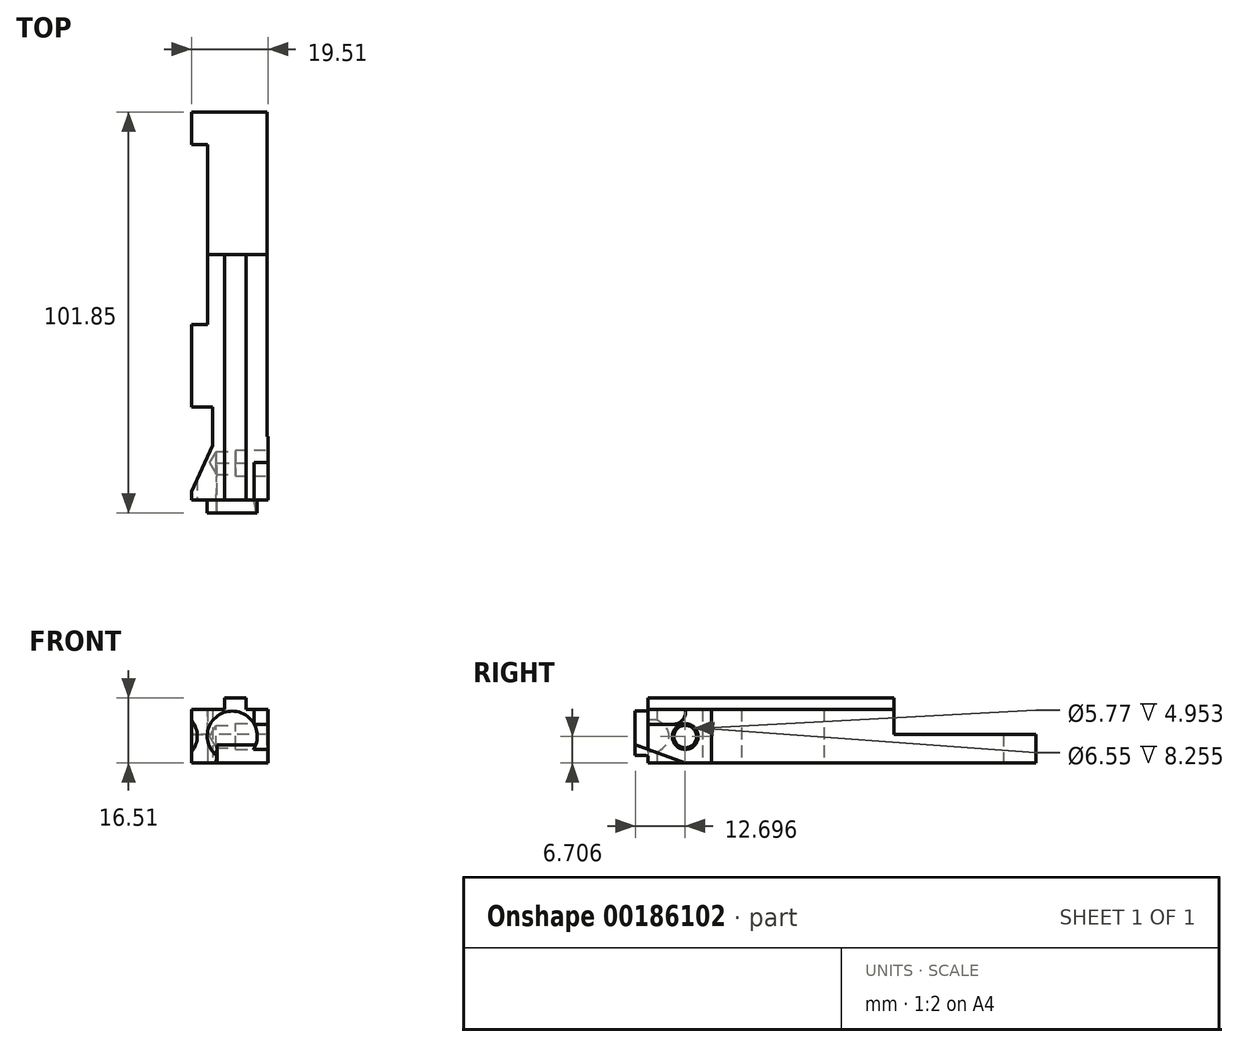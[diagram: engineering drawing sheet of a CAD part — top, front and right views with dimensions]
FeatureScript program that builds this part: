
annotation { "Feature Type Name" : "Feature", "Feature Type Description" : "" }
export const myFeature = defineFeature(function(context is Context, id is Id, definition is map)
    precondition{}
    {
        {
            var Q0;
            Q0=qCreatedBy(makeId("Front.planeOp"),FACE);
            var sketch = newSketch(context, id + "F11", { "sketchPlane" : qUnion([Q0])});
            skLineSegment(sketch, "E0.bottom", {"start": v(0, 0) * mm, "end": v(19.25, 0) * mm});
            skLineSegment(sketch, "E0.top", {"start": v(0, -16.51) * mm, "end": v(19.25, -16.51) * mm});
            skLineSegment(sketch, "E0.left", {"start": v(0, 0) * mm, "end": v(0, -16.51) * mm});
            skLineSegment(sketch, "E0.right", {"start": v(19.25, 0) * mm, "end": v(19.25, -16.51) * mm});
            skSolve(sketch);
        }
        {
            var Q0;
            Q0=makeQuery(id+"F11.imprint","IMPRINT",FACE,{"disambiguationData":[TD([[makeQuery(id+"F11.imprint","IMPRINT",EDGE,{"derivedFrom":sQuery(id+"F11.wireOp",EDGE,"E0.bottom")}),-1.0]])]});
            extrude(context, id + "F12", {"entities" : qUnion([Q0]), "depth" : 98.6 * mm});
        }
        {
            var Q0;
            Q0=makeQuery(id+"F12.opExtrude","CAP_FACE",FACE,{"disambiguationData":[OSD([sQuery(id+"F11.wireOp",EDGE,"E0.bottom"),sQuery(id+"F11.wireOp",EDGE,"E0.top"),sQuery(id+"F11.wireOp",EDGE,"E0.left"),sQuery(id+"F11.wireOp",EDGE,"E0.right")])],"isStart":false});
            var sketch = newSketch(context, id + "F0", { "sketchPlane" : qUnion([Q0])});
            skLineSegment(sketch, "E1.bottom", {"start": v(0, 0) * mm, "end": v(8.46, 0) * mm});
            skLineSegment(sketch, "E1.top", {"start": v(0, -2.92) * mm, "end": v(8.46, -2.92) * mm});
            skLineSegment(sketch, "E1.left", {"start": v(0, 0) * mm, "end": v(0, -2.92) * mm});
            skLineSegment(sketch, "E1.right", {"start": v(8.46, 0) * mm, "end": v(8.46, -2.92) * mm});
            skLineSegment(sketch, "E2.bottom", {"start": v(8.46, 0) * mm, "end": v(13.92, 0) * mm});
            skLineSegment(sketch, "E2.top", {"start": v(8.46, -2.92) * mm, "end": v(13.92, -2.92) * mm});
            skLineSegment(sketch, "E2.right", {"start": v(13.92, 0) * mm, "end": v(13.92, -2.92) * mm});
            skLineSegment(sketch, "E3.bottom", {"start": v(13.92, 0) * mm, "end": v(19.25, 0) * mm});
            skLineSegment(sketch, "E3.top", {"start": v(13.92, -2.92) * mm, "end": v(19.25, -2.92) * mm});
            skLineSegment(sketch, "E3.right", {"start": v(19.25, 0) * mm, "end": v(19.25, -2.92) * mm});
            skSolve(sketch);
        }
        {
            var Q0;
            Q0=makeQuery(id+"F0.imprint","IMPRINT",FACE,{"disambiguationData":[TD([[makeQuery(id+"F0.imprint","IMPRINT",EDGE,{"derivedFrom":sQuery(id+"F0.wireOp",EDGE,"E1.bottom")}),-1.0]])]});
            var Q1;
            Q1=makeQuery(id+"F0.imprint","IMPRINT",FACE,{"disambiguationData":[TD([[makeQuery(id+"F0.imprint","IMPRINT",EDGE,{"derivedFrom":sQuery(id+"F0.wireOp",EDGE,"E3.bottom")}),-1.0]])]});
            extrude(context, id + "F13", {"entities" : qUnion([Q0, Q1]), "operationType" : NewBodyOperationType.REMOVE, "endBound" : BoundingType.THROUGH_ALL, "oppositeDirection" : true, "depth" : 25.4 * mm});
        }
        {
            var Q0;
            Q0=makeQuery(id+"F12.opExtrude","SWEPT_FACE",FACE,{"disambiguationData":[OSD([sQuery(id+"F11.wireOp",EDGE,"E0.left")])]});
            var sketch = newSketch(context, id + "F1", { "sketchPlane" : qUnion([Q0])});
            skSolve(sketch);
        }
        {
            var Q0;
            {var subQ0=sQuery(id+"F11.wireOp",EDGE,"E0.left");Q0=makeQuery(id+"F1.imprint","IMPRINT",FACE,{"disambiguationData":[TD([[makeQuery(id+"F1.imprint","IMPRINT",EDGE,{"derivedFrom":makeQuery(id+"F12.opExtrude","CAP_EDGE",EDGE,{"disambiguationData":[OSD([subQ0])],"isStart":true})}),1.0]])]});}
            var sketch = newSketch(context, id + "F14", { "sketchPlane" : qUnion([Q0])});
            skLineSegment(sketch, "E4.bottom", {"start": v(0, 0) * mm, "end": v(36.14, 0) * mm});
            skLineSegment(sketch, "E4.top", {"start": v(0, -9.27) * mm, "end": v(36.14, -9.27) * mm});
            skLineSegment(sketch, "E4.left", {"start": v(0, 0) * mm, "end": v(0, -9.27) * mm});
            skLineSegment(sketch, "E4.right", {"start": v(36.14, 0) * mm, "end": v(36.14, -9.27) * mm});
            skSolve(sketch);
        }
        {
            var Q0;
            {var subQ0=sQuery(id+"F14.wireOp",EDGE,"E4.top");Q0=makeQuery(id+"F14.imprint","IMPRINT",FACE,{"disambiguationData":[TD([[makeQuery(id+"F14.imprint","IMPRINT",EDGE,{"derivedFrom":subQ0}),1.0]])]});}
            var Q1;
            {var subQ0=sQuery(id+"F14.wireOp",EDGE,"E4.bottom");Q1=makeQuery(id+"F14.imprint","IMPRINT",FACE,{"disambiguationData":[TD([[makeQuery(id+"F14.imprint","IMPRINT",EDGE,{"derivedFrom":subQ0}),-1.0]])]});}
            extrude(context, id + "F2", {"entities" : qUnion([Q0, Q1]), "operationType" : NewBodyOperationType.REMOVE, "endBound" : BoundingType.THROUGH_ALL, "oppositeDirection" : true, "depth" : 25.4 * mm});
        }
        {
            var Q0;
            Q0=makeQuery(id+"F12.opExtrude","SWEPT_FACE",FACE,{"disambiguationData":[OSD([sQuery(id+"F11.wireOp",EDGE,"E0.top")])]});
            var sketch = newSketch(context, id + "F15", { "sketchPlane" : qUnion([Q0])});
            skLineSegment(sketch, "E5.bottom", {"start": v(0, 53.92) * mm, "end": v(4.11, 53.92) * mm});
            skLineSegment(sketch, "E5.top", {"start": v(0, 8.26) * mm, "end": v(4.11, 8.26) * mm});
            skLineSegment(sketch, "E5.left", {"start": v(0, 53.92) * mm, "end": v(0, 8.26) * mm});
            skLineSegment(sketch, "E5.right", {"start": v(4.11, 53.92) * mm, "end": v(4.11, 8.25) * mm});
            skLineSegment(sketch, "E6.bottom", {"start": v(0, 84.76) * mm, "end": v(5.41, 84.76) * mm});
            skLineSegment(sketch, "E6.top", {"start": v(0, 74.88) * mm, "end": v(5.41, 74.88) * mm});
            skLineSegment(sketch, "E6.left", {"start": v(0, 84.76) * mm, "end": v(0, 74.88) * mm});
            skLineSegment(sketch, "E6.right", {"start": v(5.41, 84.76) * mm, "end": v(5.41, 74.88) * mm});
            skLineSegment(sketch, "E7", {"start": v(5.41, 84.76) * mm, "end": v(0, 96.36) * mm});
            skSolve(sketch);
        }
        {
            var Q0;
            {var subQ0=sQuery(id+"F15.wireOp",EDGE,"E6.bottom");Q0=makeQuery(id+"F15.imprint","IMPRINT",FACE,{"disambiguationData":[TD([[makeQuery(id+"F15.imprint","IMPRINT",EDGE,{"derivedFrom":subQ0}),1.0]])]});}
            var Q1;
            Q1=makeQuery(id+"F15.imprint","IMPRINT",FACE,{"disambiguationData":[TD([[makeQuery(id+"F15.imprint","IMPRINT",EDGE,{"derivedFrom":sQuery(id+"F15.wireOp",EDGE,"E6.bottom")}),-1.0]])]});
            var Q2;
            Q2=makeQuery(id+"F15.imprint","IMPRINT",FACE,{"disambiguationData":[TD([[makeQuery(id+"F15.imprint","IMPRINT",EDGE,{"derivedFrom":sQuery(id+"F15.wireOp",EDGE,"E5.bottom")}),-1.0]])]});
            extrude(context, id + "F3", {"entities" : qUnion([Q0, Q1, Q2]), "operationType" : NewBodyOperationType.REMOVE, "endBound" : BoundingType.THROUGH_ALL, "oppositeDirection" : true, "depth" : 25.4 * mm});
        }
        {
            var Q0;
            Q0=makeQuery(id+"F12.opExtrude","CAP_FACE",FACE,{"disambiguationData":[OSD([sQuery(id+"F11.wireOp",EDGE,"E0.bottom"),sQuery(id+"F11.wireOp",EDGE,"E0.top"),sQuery(id+"F11.wireOp",EDGE,"E0.left"),sQuery(id+"F11.wireOp",EDGE,"E0.right")])],"isStart":false});
            var sketch = newSketch(context, id + "F4", { "sketchPlane" : qUnion([Q0])});
            skCircle(sketch, "E8", {"center": v(10.36, -9.7) * mm, "radius": 6.35 * mm});
            skLineSegment(sketch, "E9", {"start": v(11.19, 0) * mm, "end": v(11.19, -3.4) * mm, "construction": true});
            skCircle(sketch, "E10", {"center": v(-4.88, -9.7) * mm, "radius": 6.35 * mm});
            skSolve(sketch);
        }
        {
            var Q0;
            {var subQ0=sQuery(id+"F4.wireOp",EDGE,"E10");var subQ1=makeQuery(id+"F12.opExtrude","CAP_EDGE",EDGE,{"disambiguationData":[OSD([sQuery(id+"F11.wireOp",EDGE,"E0.left")])],"isStart":false});var subQ2=makeQuery(id+"F4.imprint","INTERSECT",VERTEX,{"disambiguationData":[OD(0.0)],"derivedFrom":[subQ1,subQ0]});Q0=makeQuery(id+"F4.imprint","IMPRINT",FACE,{"disambiguationData":[TD([[makeQuery(id+"F4.imprint","IMPRINT",EDGE,{"disambiguationData":[TD([[subQ2,-1.0]])],"derivedFrom":subQ0}),1.0]])]});}
            extrude(context, id + "F5", {"entities" : qUnion([Q0]), "operationType" : NewBodyOperationType.REMOVE, "endBound" : BoundingType.UP_TO_NEXT, "oppositeDirection" : true, "depth" : 25.4 * mm});
        }
        {
            var Q0;
            Q0=makeQuery(id+"F4.imprint","IMPRINT",FACE,{"disambiguationData":[TD([[makeQuery(id+"F4.imprint","IMPRINT",EDGE,{"derivedFrom":sQuery(id+"F4.wireOp",EDGE,"E8")}),1.0]])]});
            extrude(context, id + "F6", {"entities" : qUnion([Q0]), "operationType" : NewBodyOperationType.ADD, "depth" : 3.25 * mm});
        }
        {
            var Q0;
            Q0=makeQuery(id+"F12.opExtrude","SWEPT_FACE",FACE,{"disambiguationData":[OSD([sQuery(id+"F11.wireOp",EDGE,"E0.right")])]});
            var sketch = newSketch(context, id + "F16", { "sketchPlane" : qUnion([Q0])});
            skLineSegment(sketch, "E11", {"start": v(-101.85, -11.89) * mm, "end": v(-89.15, -16.51) * mm});
            skLineSegment(sketch, "E12", {"start": v(-101.85, -11.89) * mm, "end": v(-101.85, -16.51) * mm});
            skLineSegment(sketch, "E13", {"start": v(-101.85, -16.51) * mm, "end": v(-89.15, -16.51) * mm});
            skLineSegment(sketch, "E14.bottom", {"start": v(-101.85, -16.51) * mm, "end": v(-82.45, -16.51) * mm});
            skLineSegment(sketch, "E14.top", {"start": v(-101.85, -2.92) * mm, "end": v(-82.45, -2.92) * mm});
            skLineSegment(sketch, "E14.left", {"start": v(-101.85, -16.51) * mm, "end": v(-101.85, -2.92) * mm});
            skLineSegment(sketch, "E14.right", {"start": v(-82.45, -16.51) * mm, "end": v(-82.45, -2.92) * mm});
            skSolve(sketch);
        }
        {
            var Q0;
            {var subQ0=sQuery(id+"F16.wireOp",EDGE,"E13");var subQ2=sQuery(id+"F11.wireOp",EDGE,"E0.right");var subQ4=makeQuery(id+"F12.opExtrude","CAP_EDGE",EDGE,{"disambiguationData":[OSD([subQ2])],"isStart":false});var subQ6=makeQuery(id+"F16.imprint","INTERSECT",VERTEX,{"derivedFrom":[subQ4,subQ0]});Q0=makeQuery(id+"F16.imprint","IMPRINT",FACE,{"disambiguationData":[TD([[makeQuery(id+"F16.imprint","IMPRINT",EDGE,{"disambiguationData":[TD([[subQ6,1.0]])],"derivedFrom":subQ4}),1.0]])]});}
            var Q1;
            {var subQ0=sQuery(id+"F16.wireOp",EDGE,"E14.left");var subQ1=sQuery(id+"F16.wireOp",EDGE,"E11");var subQ2=makeQuery(id+"F16.imprint","INTERSECT",VERTEX,{"derivedFrom":[subQ1,subQ0]});Q1=makeQuery(id+"F16.imprint","IMPRINT",FACE,{"disambiguationData":[TD([[makeQuery(id+"F16.imprint","IMPRINT",EDGE,{"disambiguationData":[TD([[subQ2,-1.0]])],"derivedFrom":subQ1}),-1.0]])]});}
            extrude(context, id + "F17", {"entities" : qUnion([Q0, Q1]), "operationType" : NewBodyOperationType.REMOVE, "oppositeDirection" : true, "depth" : 14.22 * mm});
        }
        {
            var Q0;
            Q0=makeQuery(id+"F17.boolean.opBoolean","COPY",EDGE,{"derivedFrom":makeQuery(id+"F17.opExtrude","CAP_EDGE",EDGE,{"disambiguationData":[OSD([sQuery(id+"F16.wireOp",EDGE,"E11")])],"isStart":false})});
            chamfer(context, id + "F7", {"entities" : qUnion([Q0]), "chamferType" : ChamferType.OFFSET_ANGLE, "width" : 1.52 * mm, "oppositeDirection" : false, "angle" : 85 * degree, "tangentPropagation" : true});
        }
        {
            var Q0;
            {var subQ4=sQuery(id+"F16.wireOp",EDGE,"E14.right");Q0=makeQuery(id+"F16.imprint","IMPRINT",FACE,{"disambiguationData":[TD([[makeQuery(id+"F16.imprint","IMPRINT",EDGE,{"derivedFrom":subQ4}),1.0]])]});}
            extrude(context, id + "F18", {"entities" : qUnion([Q0]), "operationType" : NewBodyOperationType.ADD, "depth" : 0.25 * mm});
        }
        {
            var Q0;
            Q0=makeQuery(id+"F18.boolean.opBoolean","MERGE",FACE,{"derivedFrom":[makeQuery(id+"F13.boolean.opBoolean","COPY",FACE,{"derivedFrom":makeQuery(id+"F13.opExtrude","SWEPT_FACE",FACE,{"disambiguationData":[OSD([sQuery(id+"F0.wireOp",EDGE,"E3.top")])]})}),makeQuery(id+"F18.opExtrude","SWEPT_FACE",FACE,{"disambiguationData":[OSD([sQuery(id+"F16.wireOp",EDGE,"E14.top")])]})]});
            var sketch = newSketch(context, id + "F8", { "sketchPlane" : qUnion([Q0])});
            skLineSegment(sketch, "E15.bottom", {"start": v(19.5, -98.6) * mm, "end": v(15.95, -98.6) * mm});
            skLineSegment(sketch, "E15.top", {"start": v(19.5, -89.08) * mm, "end": v(15.95, -89.08) * mm});
            skLineSegment(sketch, "E15.left", {"start": v(19.5, -98.6) * mm, "end": v(19.5, -89.08) * mm});
            skLineSegment(sketch, "E15.right", {"start": v(15.95, -98.6) * mm, "end": v(15.95, -89.08) * mm});
            skSolve(sketch);
        }
        {
            var Q0;
            Q0=makeQuery(id+"F8.imprint","IMPRINT",FACE,{"disambiguationData":[TD([[makeQuery(id+"F8.imprint","IMPRINT",EDGE,{"derivedFrom":sQuery(id+"F8.wireOp",EDGE,"E15.bottom")}),1.0]])]});
            extrude(context, id + "F9", {"entities" : qUnion([Q0]), "operationType" : NewBodyOperationType.REMOVE, "oppositeDirection" : true, "depth" : 3.8 * mm});
        }
        {
            var Q0;
            Q0=makeQuery(id+"F9.boolean.opBoolean","COPY",EDGE,{"derivedFrom":makeQuery(id+"F9.opExtrude","CAP_EDGE",EDGE,{"disambiguationData":[OSD([sQuery(id+"F8.wireOp",EDGE,"E15.top")])],"isStart":false})});
            fillet(context, id + "F19", {"entities" : qUnion([Q0]), "radius" : 3.17 * mm, "tangentPropagation" : true, "allowEdgeOverflow" : false});
        }
        {
            var Q0;
            Q0=makeQuery(id+"F18.opExtrude","CAP_FACE",FACE,{"disambiguationData":[OSD([sQuery(id+"F11.wireOp",EDGE,"E0.right"),sQuery(id+"F16.wireOp",EDGE,"E11"),sQuery(id+"F16.wireOp",EDGE,"E14.bottom"),sQuery(id+"F16.wireOp",EDGE,"E14.top"),sQuery(id+"F16.wireOp",EDGE,"E14.right")])],"isStart":false});
            var sketch = newSketch(context, id + "F10", { "sketchPlane" : qUnion([Q0])});
            skPoint(sketch, "E16", {"position": v(-89.15, -9.8) * mm});
            skSolve(sketch);
        }
        {
            var Q0;
            Q0=sQuery(id+"F10.wireOp",VERTEX,"E16");
            var Q1;
            Q1=makeQuery(id+"F12.opExtrude","SWEPT_BODY",BODY,{"disambiguationData":[OSD([sQuery(id+"F11.wireOp",EDGE,"E0.bottom"),sQuery(id+"F11.wireOp",EDGE,"E0.top"),sQuery(id+"F11.wireOp",EDGE,"E0.left"),sQuery(id+"F11.wireOp",EDGE,"E0.right")])]});
            hole(context, id + "F20", {"style" : HoleStyle.C_BORE, "endStyle" : HoleEndStyle.BLIND, "standardTappedOrClearance" : lookupTablePath({ "fit" : "Normal (ASME)", "standard" : "ANSI", "size" : "#10" }), "standardBlindInLast" : lookupTablePath({ "fit" : "Free", "standard" : "ANSI", "size" : "#10" }), "holeDiameter" : 5.77 * mm, "cBoreDiameter" : 6.55 * mm, "cBoreDepth" : 8.25 * mm, "holeDepth" : 13.2 * mm, "locations" : qUnion([Q0]), "scope" : qUnion([Q1])});
        }
    });
